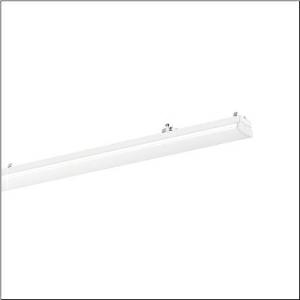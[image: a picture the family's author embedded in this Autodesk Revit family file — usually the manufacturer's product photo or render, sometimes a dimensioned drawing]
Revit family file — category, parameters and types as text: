
# Revit family: licross_r__11_recessed_opal_ho_51te1dcn4cxm_dbf2
name_source: partatom
category: Lighting Fixtures
units: mm (PartAtom-declared; Revit-internal decimal feet)

## family parameters
Cut with Voids When Loaded = No
Host = Face
Light Source = No
Part Type = Normal
Room Calculation Point = No
Round Connector Dimension = Use Diameter
Shared = No

## types (1)
- --- (1 x LED, 12370 lm, 66.5 W, 4000K)
    Apparent Load = 67 VA
    CIE Flux Codes = 44 73 91 87 100
    Color Rendering = 80
    Color Temperature = 4000K
    Default Elevation = 1800 mm
    Description = Licross® 11 recessed opal HO, luminaire insert, of sheet steel, coil coated, white, length: 1.500mm, width: 76mm, height: 87mm, LED rated luminous flux: 12.370lm, light colour: 840, control gear: ON/OFF Multilumen, CLOi, with plug, 3-pole, with phase selection, mains connection: 220..240V, AC, 50/60Hz, start of lifetime: 67W, end of service life: 75W, internal wiring halogen-free, primary optical cover: cover, of PMMA, light emission: direct with ceiling illumination distribution, primary light characteristic: symmetric, protection rating (complete): IP54, insulation class (complete): insulation class I (protective earthing), certification: CE, ENEC, VDE, UKCA, protection symbol: D if used in an environment with non-conductive dust loads with corresponding accessories, impact resistance: IK06, permissible ambient temperature for indoor applications: -35..+35°C, corresponds to IFS (International Featured Standards) requirements for safety and quality in the food industry, reducing of maximum allowable ambient temperature of 5°C with ceiling mounting, LABS conformity tested according to VDMA 24364:2018-05, packaging unit: 1 piece
    Height = 83 mm
    Lamp = 1 x LED
    Lamp Light Flux = 12370 lm
    Lamp Power = 66.5 W
    Lamp count = 1
    Length = 1500 mm
    Luminous efficacy = 186 lm/W
    Manufacturer = Siteco
    ModVariant = No
    Model = 51TE1DCN4CXM
    Mounting Place = Ceiling
    Mounting Type = Pendant
    Number of Poles = 1
    OnlyDefault = Yes
    Power Factor = 1
    Product Name = Licross® 11 recessed opal HO
    Product group = luminaire insert | ceiling pendant
    ProductGroupID = 902
    Protection Class = Protection class I
    Protection Degree = IP 54
    RLX_Detail_Level = 1
    RLX_Emergency_Light_Flux = 0 lm
    RLX_Emergency_Type = 0
    RLX_Emergency_Type_DB = No
    RlxData = <blob elided: 24609 chars, md5=844fa2af>
    Socket = socket
    Standby Power = 0 W
    System Light Flux = 12370 lm
    System Power = 67 W
    Type Comments = factory setting: luminous flux: 100 % | (A | C | E) | 156 mA
    Type Image = l_1313666.jpg
    URL = http://relux.com
    VarID = @adj_089845
    Voltage = 0 V
    Weight = 0.00 kg
    Width = 76 mm

## geometry (parser evidence)
native form markers: Blend x4, Sweep x13
no freeform markers — native parametric forms only
